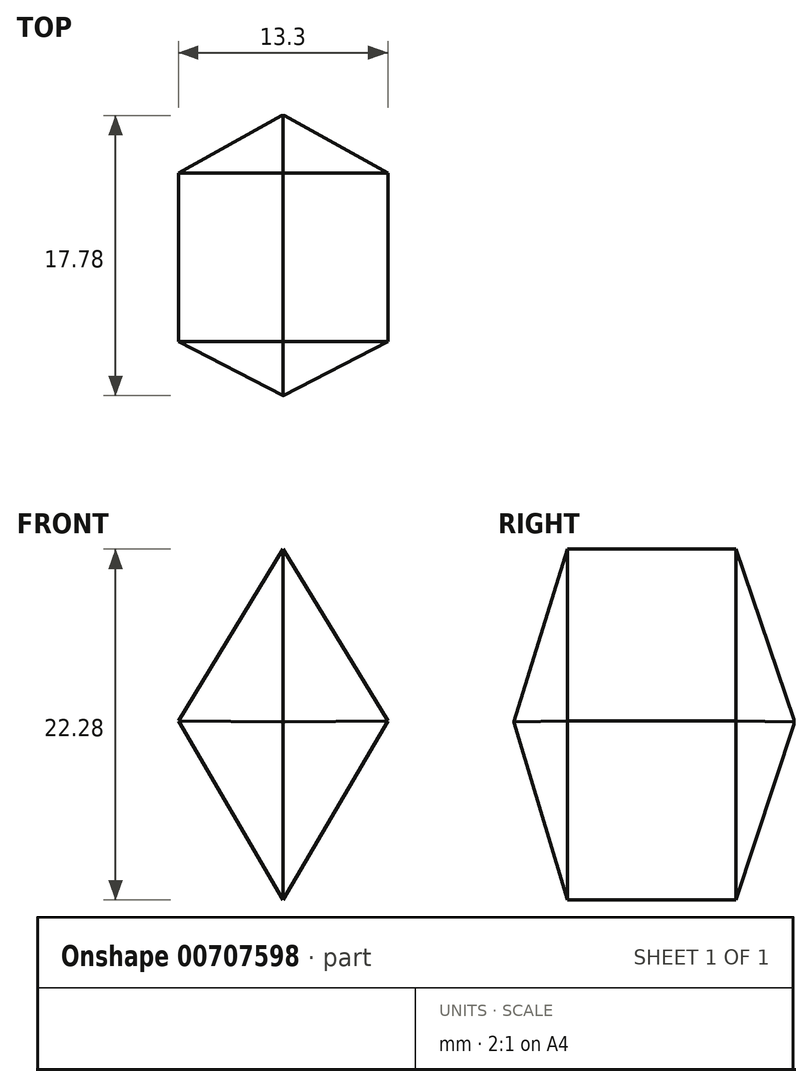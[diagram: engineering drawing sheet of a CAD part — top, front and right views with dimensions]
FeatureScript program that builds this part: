
annotation { "Feature Type Name" : "Feature", "Feature Type Description" : "" }
export const myFeature = defineFeature(function(context is Context, id is Id, definition is map)
    precondition{}
    {
        {
            var Q0;
            Q0=qCreatedBy(makeId("Front.planeOp"),FACE);
            var sketch = newSketch(context, id + "F0", { "sketchPlane" : qUnion([Q0])});
            skLineSegment(sketch, "E0", {"start": v(11.7, 8.56) * mm, "end": v(10.7, -7.18) * mm});
            skLineSegment(sketch, "E1", {"start": v(10.7, -7.18) * mm, "end": v(-10.6, 19) * mm});
            skLineSegment(sketch, "E2", {"start": v(-10.6, 19) * mm, "end": v(-7.8, 82.36) * mm});
            skFitSpline(sketch, "E3", {"points": [v(-7.8, 82.36) * mm, v(-7.24, 98.94) * mm, v(-6.59, 117.12) * mm, v(-5.83, 142.02) * mm, v(-5.45, 168.32) * mm, v(-5.52, 230.34) * mm, v(-6.26, 285.7) * mm, v(-7.2, 315.28) * mm, v(-8.95, 361.43) * mm, v(-10.4, 387.63) * mm, v(-13, 416.84) * mm, v(-15.01, 437.7) * mm, v(-21.29, 480.96) * mm, v(-27.2, 508.68) * mm, v(-28.7, 514.88) * mm], "startDerivative": vector(10.22, 308.11) * mm, "endDerivative": vector(-37.95, 155.7) * mm});
            skLineSegment(sketch, "E4", {"start": v(-28.7, 514.88) * mm, "end": v(-18.5, 504.49) * mm});
            skFitSpline(sketch, "E5", {"points": [v(-18.5, 504.49) * mm, v(-14.2, 494.72) * mm, v(-10.4, 483.17) * mm, v(-6.54, 469.9) * mm, v(-3.1, 457.05) * mm, v(-0.51, 445.6) * mm, v(1.47, 435.93) * mm, v(2.96, 426.2) * mm, v(4.35, 415.6) * mm, v(5.85, 403.15) * mm, v(7.18, 390.92) * mm, v(9.67, 369.53) * mm, v(11.56, 352.56) * mm, v(15.2, 318.42) * mm, v(18.03, 290.8) * mm, v(19.92, 265.34) * mm, v(21.72, 242.6) * mm, v(22.69, 220.79) * mm, v(23.65, 203.25) * mm, v(24.47, 178.85) * mm, v(25.08, 148.77) * mm, v(25.19, 106.94) * mm, v(24.82, 74.57) * mm, v(24.5, 42) * mm], "startDerivative": vector(138.63, -295.52) * mm, "endDerivative": vector(-5.12, -584.15) * mm});
            skFitSpline(sketch, "E6", {"points": [v(24.5, 42) * mm, v(16.7, 39) * mm, v(12.5, 33.24) * mm, v(9.61, 24.95) * mm, v(8.9, 16.91) * mm, v(10.33, 12.23) * mm, v(11.7, 8.56) * mm], "startDerivative": vector(-46.28, -12) * mm, "endDerivative": vector(10.21, -28.51) * mm});
            skFitSpline(sketch, "E7", {"points": [v(-10.6, 84.98) * mm, v(-8.5, 83) * mm, v(-6.65, 78.8) * mm, v(-5.89, 72.07) * mm, v(-5.76, 61.33) * mm, v(-5.64, 47.1) * mm, v(-5.9, 35.6) * mm, v(-6.47, 31.43) * mm, v(-6.34, 26.97) * mm, v(-4.57, 21.8) * mm, v(-2.21, 17.83) * mm, v(0, 15.05) * mm, v(2.28, 13.08) * mm, v(5.76, 11.32) * mm, v(8.69, 10.16) * mm, v(11.04, 8.9) * mm, v(12.38, 7.6) * mm, v(13.09, 5.99) * mm, v(12.89, 2.76) * mm, v(12.15, -3.9) * mm, v(11.7, -8.74) * mm, v(11.08, -13.22) * mm], "startDerivative": vector(59.9, -45.86) * mm, "endDerivative": vector(-14.62, -97.53) * mm});
            skLineSegment(sketch, "E8", {"start": v(11.08, -13.22) * mm, "end": v(11.08, -15.97) * mm});
            skLineSegment(sketch, "E9", {"start": v(11.08, -15.97) * mm, "end": v(-11.03, -15.97) * mm});
            skLineSegment(sketch, "E10", {"start": v(-11.03, -15.97) * mm, "end": v(-11.2, -13.29) * mm});
            skFitSpline(sketch, "E11", {"points": [v(-11.2, -13.29) * mm, v(-11.2, -11.84) * mm, v(-11.2, -5.52) * mm, v(-11.51, 1.49) * mm, v(-12.16, 4.66) * mm, v(-13.4, 9.05) * mm, v(-15.15, 13.55) * mm, v(-16.64, 17.33) * mm, v(-19.12, 23.61) * mm, v(-19.55, 26.56) * mm, v(-18.64, 31.28) * mm, v(-16.79, 35.33) * mm, v(-14.77, 40.57) * mm, v(-13.5, 46.17) * mm, v(-12.6, 53.4) * mm, v(-12.2, 59.96) * mm, v(-12.37, 65.97) * mm, v(-12.16, 73.91) * mm, v(-11.5, 81.04) * mm, v(-11.2, 84.64) * mm, v(-10.6, 84.98) * mm], "startDerivative": vector(-0.12, 43.3) * mm, "endDerivative": vector(35.61, 8.6) * mm});
            skFitSpline(sketch, "E12", {"points": [v(11.08, -13.22) * mm, v(15.57, -17.52) * mm, v(22.06, -24.41) * mm, v(29.6, -33.47) * mm, v(35.84, -41.56) * mm, v(40.17, -47.64) * mm, v(44.57, -55.74) * mm, v(47.94, -62.06) * mm, v(51.06, -67.51) * mm, v(52.42, -69.67) * mm, v(49.81, -81.38) * mm, v(45.5, -94.07) * mm, v(41.24, -106.63) * mm, v(36.2, -120.43) * mm, v(32.84, -130.03) * mm, v(29.35, -138.2) * mm, v(27.78, -142.23) * mm, v(23.27, -152.08) * mm, v(21.3, -154.75) * mm, v(16.02, -157.43) * mm, v(8.58, -160.03) * mm, v(4.77, -160.41) * mm, v(4.83, -154.75) * mm, v(8.26, -152.78) * mm, v(13.03, -150.3) * mm, v(16.97, -147.44) * mm, v(20.66, -141.85) * mm, v(25.37, -129.07) * mm, v(31.66, -108.36) * mm, v(36.51, -89.69) * mm, v(39.56, -77.02) * mm, v(39.75, -72.83) * mm, v(38.74, -67.42) * mm, v(35.21, -61.22) * mm, v(28.26, -50.55) * mm, v(23.02, -43.89) * mm, v(18.43, -38.21) * mm, v(13.22, -32.69) * mm, v(7.93, -27.32) * mm, v(6.6, -20.94) * mm, v(11.08, -13.22) * mm]});
            skLineSegment(sketch, "E13.bottom", {"start": v(-12.44, -13.29) * mm, "end": v(11.54, -13.29) * mm});
            skLineSegment(sketch, "E13.top", {"start": v(-12.44, -29.01) * mm, "end": v(11.54, -29.01) * mm});
            skLineSegment(sketch, "E13.left", {"start": v(-12.44, -13.29) * mm, "end": v(-12.44, -29.01) * mm});
            skLineSegment(sketch, "E13.right", {"start": v(11.54, -13.29) * mm, "end": v(11.54, -29.01) * mm});
            skLineSegment(sketch, "E14", {"start": v(0, -32.56) * mm, "end": v(0, -38.28) * mm});
            skFitSpline(sketch, "E15", {"points": [v(-10.75, -28.03) * mm, v(-9.93, -35.6) * mm, v(-9.25, -45.2) * mm, v(-8.25, -64.06) * mm, v(-7.6, -83.45) * mm, v(-7.55, -95.02) * mm, v(-7.45, -109.5) * mm, v(-7.73, -122.65) * mm, v(-8.29, -138.57) * mm, v(-9.14, -152.56) * mm, v(-9.03, -155.04) * mm], "startDerivative": vector(11.05, -94.6) * mm, "endDerivative": vector(4.37, -43.01) * mm});
            skLineSegment(sketch, "E16", {"start": v(-9.9, -153.6) * mm, "end": v(9.57, -153.6) * mm});
            skFitSpline(sketch, "E17.MirrorCS", {"points": [v(10.75, -28.03) * mm, v(9.93, -35.6) * mm, v(9.25, -45.2) * mm, v(8.25, -64.06) * mm, v(7.6, -83.45) * mm, v(7.55, -95.02) * mm, v(7.45, -109.5) * mm, v(7.73, -122.65) * mm, v(8.29, -138.57) * mm, v(9.14, -152.56) * mm, v(9.03, -155.04) * mm], "startDerivative": vector(-11.05, -94.6) * mm, "endDerivative": vector(-4.37, -43.01) * mm});
            skSolve(sketch);
        }
        {
            var Q0;
            {var subQ4=sQuery(id+"F0.wireOp",EDGE,"E1");Q0=makeQuery(id+"F0.imprint","IMPRINT",FACE,{"disambiguationData":[TD([[makeQuery(id+"F0.imprint","IMPRINT",EDGE,{"derivedFrom":subQ4}),1.0]])]});}
            var Q1;
            {var subQ0=sQuery(id+"F0.wireOp",EDGE,"E1");Q1=makeQuery(id+"F0.imprint","IMPRINT",FACE,{"disambiguationData":[TD([[makeQuery(id+"F0.imprint","IMPRINT",EDGE,{"derivedFrom":subQ0}),-1.0]])]});}
            var Q2;
            {var subQ0=sQuery(id+"F0.wireOp",EDGE,"E9");var subQ1=sQuery(id+"F0.wireOp",EDGE,"E8");var subQ2=makeQuery(id+"F0.imprint","INTERSECT",VERTEX,{"derivedFrom":[subQ1,subQ0]});Q2=makeQuery(id+"F0.imprint","IMPRINT",FACE,{"disambiguationData":[TD([[makeQuery(id+"F0.imprint","IMPRINT",EDGE,{"disambiguationData":[TD([[subQ2,1.0]])],"derivedFrom":subQ1}),-1.0]])]});}
            var Q3;
            {var subQ0=sQuery(id+"F0.wireOp",EDGE,"E10");Q3=makeQuery(id+"F0.imprint","IMPRINT",FACE,{"disambiguationData":[TD([[makeQuery(id+"F0.imprint","IMPRINT",EDGE,{"derivedFrom":subQ0}),-1.0]])]});}
            var Q4;
            {var subQ1=sQuery(id+"F0.wireOp",EDGE,"E8");var subQ3=sQuery(id+"F0.wireOp",EDGE,"E13.bottom");var subQ4=makeQuery(id+"F0.imprint","INTERSECT",VERTEX,{"derivedFrom":[subQ1,subQ3]});Q4=makeQuery(id+"F0.imprint","IMPRINT",FACE,{"disambiguationData":[TD([[makeQuery(id+"F0.imprint","IMPRINT",EDGE,{"disambiguationData":[TD([[subQ4,1.0]])],"derivedFrom":subQ3}),1.0]])]});}
            extrude(context, id + "F1", {"entities" : qUnion([Q0, Q1, Q2, Q3, Q4]), "depth" : 5.08 * mm, "offsetDistance" : 25.4 * mm});
        }
        {
            var Q0;
            Q0=makeQuery(id+"F1.opExtrude","CAP_FACE",FACE,{"disambiguationData":[OSD([sQuery(id+"F0.wireOp",EDGE,"E7"),sQuery(id+"F0.wireOp",EDGE,"E11"),sQuery(id+"F0.wireOp",EDGE,"E12"),sQuery(id+"F0.wireOp",EDGE,"E13.bottom")])],"isStart":true});
            extrude(context, id + "F2", {"entities" : qUnion([Q0]), "operationType" : NewBodyOperationType.ADD, "depth" : 5.08 * mm, "offsetDistance" : 25.4 * mm});
        }
        {
            var Q0;
            Q0=makeQuery(id+"F1.opExtrude","CAP_FACE",FACE,{"disambiguationData":[OSD([sQuery(id+"F0.wireOp",EDGE,"E7"),sQuery(id+"F0.wireOp",EDGE,"E8"),sQuery(id+"F0.wireOp",EDGE,"E9"),sQuery(id+"F0.wireOp",EDGE,"E10"),sQuery(id+"F0.wireOp",EDGE,"E11")])],"isStart":false});
            var sketch = newSketch(context, id + "F3", { "sketchPlane" : qUnion([Q0])});
            skLineSegment(sketch, "E18", {"start": v(0, 13) * mm, "end": v(7.67, 0) * mm});
            skLineSegment(sketch, "E19", {"start": v(7.67, 0) * mm, "end": v(0, -13) * mm});
            skLineSegment(sketch, "E20", {"start": v(0, -13) * mm, "end": v(0, -9.64) * mm});
            skLineSegment(sketch, "E21.MirrorCS", {"start": v(-7.67, 0) * mm, "end": v(0, -13) * mm});
            skLineSegment(sketch, "E22.MirrorCS", {"start": v(0, 13) * mm, "end": v(-7.67, 0) * mm});
            skLineSegment(sketch, "E23.bottom", {"start": v(-55.21, 97.24) * mm, "end": v(69.67, 97.24) * mm});
            skLineSegment(sketch, "E23.top", {"start": v(-55.21, -36.84) * mm, "end": v(69.67, -36.84) * mm});
            skLineSegment(sketch, "E23.left", {"start": v(-55.21, 97.24) * mm, "end": v(-55.21, -36.84) * mm});
            skLineSegment(sketch, "E23.right", {"start": v(69.67, 97.24) * mm, "end": v(69.67, -36.84) * mm});
            skSolve(sketch);
        }
        {
            var Q0;
            Q0=makeQuery(id+"F3.imprint","IMPRINT",FACE,{"disambiguationData":[TD([[makeQuery(id+"F3.imprint","IMPRINT",EDGE,{"derivedFrom":sQuery(id+"F3.wireOp",EDGE,"E23.bottom")}),-1.0]])]});
            var Q1;
            Q1=makeQuery(id+"F3.imprint","IMPRINT",FACE,{"disambiguationData":[TD([[makeQuery(id+"F3.imprint","IMPRINT",EDGE,{"derivedFrom":sQuery(id+"F3.wireOp",EDGE,"E18")}),1.0]])]});
            extrude(context, id + "F4", {"entities" : qUnion([Q0, Q1]), "operationType" : NewBodyOperationType.REMOVE, "oppositeDirection" : true, "depth" : 25.4 * mm, "offsetDistance" : 25.4 * mm});
        }
        {
            var Q0;
            Q0=makeQuery(id+"F1.opExtrude","CAP_FACE",FACE,{"disambiguationData":[OSD([sQuery(id+"F0.wireOp",EDGE,"E7"),sQuery(id+"F0.wireOp",EDGE,"E8"),sQuery(id+"F0.wireOp",EDGE,"E9"),sQuery(id+"F0.wireOp",EDGE,"E10"),sQuery(id+"F0.wireOp",EDGE,"E11")])],"isStart":false});
            extrude(context, id + "F5", {"entities" : qUnion([Q0]), "operationType" : NewBodyOperationType.ADD, "depth" : 1.27 * mm, "offsetDistance" : 25.4 * mm});
        }
        {
            var Q0;
            Q0=makeQuery(id+"F2.opExtrude","CAP_FACE",FACE,{"disambiguationData":[OSD([sQuery(id+"F0.wireOp",EDGE,"E7"),sQuery(id+"F0.wireOp",EDGE,"E8"),sQuery(id+"F0.wireOp",EDGE,"E9"),sQuery(id+"F0.wireOp",EDGE,"E10"),sQuery(id+"F0.wireOp",EDGE,"E11")])],"isStart":false});
            extrude(context, id + "F6", {"entities" : qUnion([Q0]), "operationType" : NewBodyOperationType.ADD, "depth" : 1.27 * mm, "offsetDistance" : 25.4 * mm});
        }
        {
            var Q0;
            Q0=makeQuery(id+"F5.opExtrude","CAP_FACE",FACE,{"disambiguationData":[OSD([sQuery(id+"F0.wireOp",EDGE,"E7"),sQuery(id+"F0.wireOp",EDGE,"E8"),sQuery(id+"F0.wireOp",EDGE,"E9"),sQuery(id+"F0.wireOp",EDGE,"E10"),sQuery(id+"F0.wireOp",EDGE,"E11")])],"isStart":false});
            var sketch = newSketch(context, id + "F7", { "sketchPlane" : qUnion([Q0])});
            skLineSegment(sketch, "E24", {"start": v(0, 10.93) * mm, "end": v(-6.65, 0) * mm});
            skLineSegment(sketch, "E25", {"start": v(-6.65, 0) * mm, "end": v(0, -11.35) * mm});
            skLineSegment(sketch, "E26", {"start": v(0, -11.35) * mm, "end": v(0, -8.42) * mm});
            skLineSegment(sketch, "E27.MirrorCS", {"start": v(6.65, 0) * mm, "end": v(0, -11.35) * mm});
            skLineSegment(sketch, "E28.MirrorCS", {"start": v(0, 10.93) * mm, "end": v(6.65, 0) * mm});
            skSolve(sketch);
        }
        {
            var Q0;
            Q0=makeQuery(id+"F7.imprint","IMPRINT",FACE,{"disambiguationData":[TD([[makeQuery(id+"F7.imprint","IMPRINT",EDGE,{"derivedFrom":sQuery(id+"F7.wireOp",EDGE,"E24")}),-1.0]])]});
            extrude(context, id + "F8", {"entities" : qUnion([Q0]), "operationType" : NewBodyOperationType.REMOVE, "oppositeDirection" : true, "depth" : 25.4 * mm, "offsetDistance" : 25.4 * mm});
        }
        {
            var Q0;
            Q0=makeQuery(id+"F5.opExtrude","CAP_FACE",FACE,{"disambiguationData":[OSD([sQuery(id+"F0.wireOp",EDGE,"E7"),sQuery(id+"F0.wireOp",EDGE,"E8"),sQuery(id+"F0.wireOp",EDGE,"E9"),sQuery(id+"F0.wireOp",EDGE,"E10"),sQuery(id+"F0.wireOp",EDGE,"E11")])],"isStart":false});
            extrude(context, id + "F9", {"entities" : qUnion([Q0]), "operationType" : NewBodyOperationType.ADD, "depth" : 2.54 * mm, "offsetDistance" : 25.4 * mm});
        }
        {
            var Q0;
            Q0=makeQuery(id+"F6.opExtrude","CAP_FACE",FACE,{"disambiguationData":[OSD([sQuery(id+"F0.wireOp",EDGE,"E7"),sQuery(id+"F0.wireOp",EDGE,"E8"),sQuery(id+"F0.wireOp",EDGE,"E9"),sQuery(id+"F0.wireOp",EDGE,"E10"),sQuery(id+"F0.wireOp",EDGE,"E11")])],"isStart":false});
            extrude(context, id + "F10", {"entities" : qUnion([Q0]), "operationType" : NewBodyOperationType.ADD, "depth" : 2.54 * mm, "offsetDistance" : 25.4 * mm});
        }
        {
            var Q0;
            Q0=makeQuery(id+"F9.opExtrude","CAP_FACE",FACE,{"disambiguationData":[OSD([sQuery(id+"F0.wireOp",EDGE,"E7"),sQuery(id+"F0.wireOp",EDGE,"E8"),sQuery(id+"F0.wireOp",EDGE,"E9"),sQuery(id+"F0.wireOp",EDGE,"E10"),sQuery(id+"F0.wireOp",EDGE,"E11")])],"isStart":false});
            chamfer(context, id + "F11", {"entities" : qUnion([Q0]), "chamferType" : ChamferType.OFFSET_ANGLE, "width" : 5.7 * mm, "oppositeDirection" : false, "angle" : 31 * degree, "tangentPropagation" : true});
        }
        {
            var Q0;
            Q0=makeQuery(id+"F10.opExtrude","CAP_FACE",FACE,{"disambiguationData":[OSD([sQuery(id+"F0.wireOp",EDGE,"E7"),sQuery(id+"F0.wireOp",EDGE,"E8"),sQuery(id+"F0.wireOp",EDGE,"E9"),sQuery(id+"F0.wireOp",EDGE,"E10"),sQuery(id+"F0.wireOp",EDGE,"E11")])],"isStart":false});
            chamfer(context, id + "F12", {"entities" : qUnion([Q0]), "chamferType" : ChamferType.OFFSET_ANGLE, "width" : 3.66 * mm, "oppositeDirection" : false, "angle" : 57 * degree, "tangentPropagation" : true});
        }
    });
